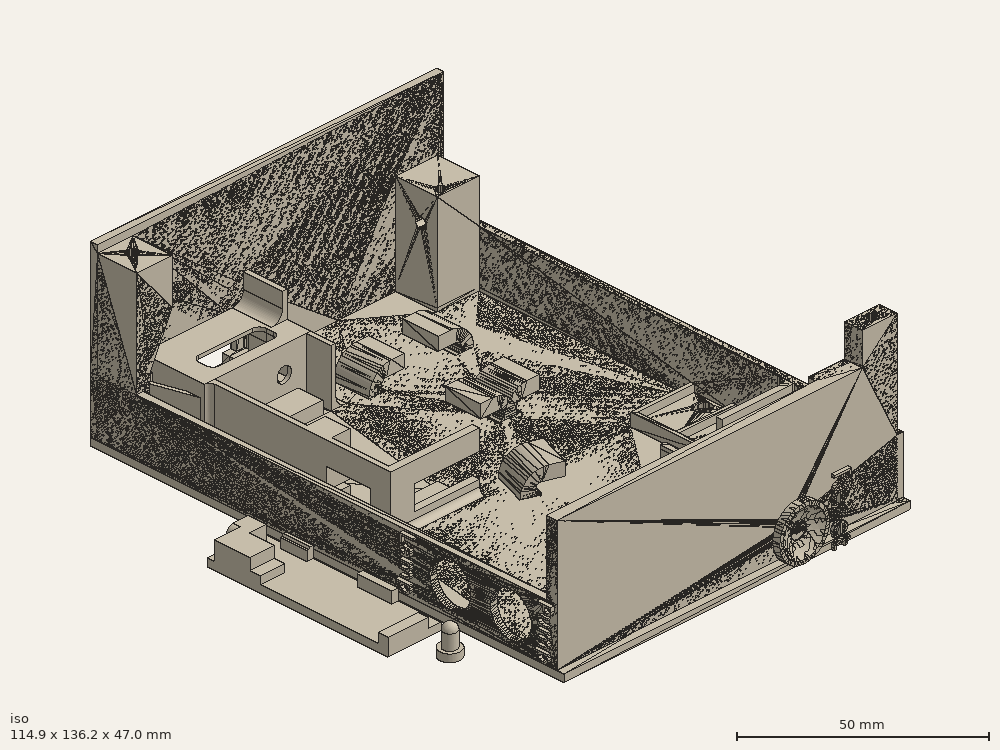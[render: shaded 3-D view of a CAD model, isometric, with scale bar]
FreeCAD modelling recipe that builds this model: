
FCSTD DOCUMENT  (FreeCAD 0.18.4R)
Label: tmp
License: All rights reserved
LicenseURL: http://en.wikipedia.org/wiki/All_rights_reserved
objects: Part::FeaturePython×102, Part::MultiFuse×20, Part::Part2DObjectPython×9, Part::Cut×8, Part::Extrusion×5, Part::Feature×5, App::DocumentObjectGroup×5, Part::Cone×4, Part::Fuse×1
note: 154 computed .brp shape members not serialized (recipe doc carries the construction recipe); baked Part::Feature solids carry a one-line shape summary decoded from their .brp

FEATURE [Part::FeaturePython] Slice002_child0  label="Slice002.0"  # WARN: FeaturePython — macro-defined, semantics opaque (R4)
  FilterType = 1
  Invert = false
  OverrideMaxVal = 0
  WindowFrom = 80
  WindowTo = 100
  items = 0
FEATURE [Part::FeaturePython] Slice005_child0  label="Slice005.0"  # WARN: FeaturePython — macro-defined, semantics opaque (R4)
  FilterType = 1
  Invert = false
  OverrideMaxVal = 0
  WindowFrom = 80
  WindowTo = 100
  items = 0
FEATURE [Part::Part2DObjectPython] Rectangle  # Draft 2D object (typed FeaturePython)
  ChamferSize = 0
  Columns = 1
  FilletRadius = 0
  Height = 55
  Length = 179
  MakeFace = true
  Placement = pos=(42.6826,-163.503,-171.403) rot=(-1,0,0;1.5708rad)
  Rows = 1
  Support = -> [Slice005_child0]
FEATURE [Part::FeaturePython] Slice  # WARN: FeaturePython — macro-defined, semantics opaque (R4)
  Base = -> Slice005_child0
  Mode = 1
  Tolerance = 0
  Tools = -> [Rectangle]
FEATURE [Part::FeaturePython] Slice_child0  label="Slice.0"  # WARN: FeaturePython — macro-defined, semantics opaque (R4)
  Base = -> Slice
  FilterType = 1
  Invert = false
  OverrideMaxVal = 0
  WindowFrom = 80
  WindowTo = 100
  items = 0
FEATURE [Part::FeaturePython] Slice_child1  label="Slice.1"  # WARN: FeaturePython — macro-defined, semantics opaque (R4)
  Base = -> Slice
  FilterType = 1
  Invert = false
  OverrideMaxVal = 0
  WindowFrom = 80
  WindowTo = 100
  items = 1
FEATURE [Part::FeaturePython] Slice_child2  label="Slice.2"  # WARN: FeaturePython — macro-defined, semantics opaque (R4)
  Base = -> Slice
  FilterType = 1
  Invert = false
  OverrideMaxVal = 0
  WindowFrom = 80
  WindowTo = 100
  items = 2
FEATURE [Part::FeaturePython] Slice003_child0  label="Side.1"  # WARN: FeaturePython — macro-defined, semantics opaque (R4)
  FilterType = 1
  Invert = false
  OverrideMaxVal = 0
  WindowFrom = 80
  WindowTo = 100
  items = 0
FEATURE [Part::FeaturePython] Slice002_child001  label="Slice002.001"  # WARN: FeaturePython — macro-defined, semantics opaque (R4)
  FilterType = 1
  Invert = false
  OverrideMaxVal = 0
  WindowFrom = 80
  WindowTo = 100
  items = 0
FEATURE [Part::FeaturePython] Slice_child5  label="Slice.5"  # WARN: FeaturePython — macro-defined, semantics opaque (R4)
  Base = -> Slice
  FilterType = 1
  Invert = false
  OverrideMaxVal = 0
  WindowFrom = 80
  WindowTo = 100
  items = 5
FEATURE [Part::FeaturePython] Slice_child8  label="Slice.8"  # WARN: FeaturePython — macro-defined, semantics opaque (R4)
  Base = -> Slice
  FilterType = 1
  Invert = false
  OverrideMaxVal = 0
  WindowFrom = 80
  WindowTo = 100
  items = 8
FEATURE [Part::FeaturePython] Slice_child009  label="Slice.009"  # WARN: FeaturePython — macro-defined, semantics opaque (R4)
  Base = -> Slice
  FilterType = 1
  Invert = false
  OverrideMaxVal = 0
  WindowFrom = 80
  WindowTo = 100
  items = 1
FEATURE [Part::FeaturePython] Slice_child3  label="Slice.3"  # WARN: FeaturePython — macro-defined, semantics opaque (R4)
  Base = -> Slice
  FilterType = 1
  Invert = false
  OverrideMaxVal = 0
  WindowFrom = 80
  WindowTo = 100
  items = 3
FEATURE [Part::FeaturePython] Slice002_child002  label="Slice002.002"  # WARN: FeaturePython — macro-defined, semantics opaque (R4)
  FilterType = 1
  Invert = false
  OverrideMaxVal = 0
  WindowFrom = 80
  WindowTo = 100
  items = 0
FEATURE [Part::FeaturePython] Slice_child6  label="Slice.6"  # WARN: FeaturePython — macro-defined, semantics opaque (R4)
  Base = -> Slice
  FilterType = 1
  Invert = false
  OverrideMaxVal = 0
  WindowFrom = 80
  WindowTo = 100
  items = 6
FEATURE [Part::FeaturePython] Slice_child7  label="Slice.7"  # WARN: FeaturePython — macro-defined, semantics opaque (R4)
  Base = -> Slice
  FilterType = 1
  Invert = false
  OverrideMaxVal = 0
  WindowFrom = 80
  WindowTo = 100
  items = 7
FEATURE [Part::FeaturePython] Slice_child010  label="Slice.010"  # WARN: FeaturePython — macro-defined, semantics opaque (R4)
  Base = -> Slice
  FilterType = 1
  Invert = false
  OverrideMaxVal = 0
  WindowFrom = 80
  WindowTo = 100
  items = 2
FEATURE [Part::FeaturePython] Slice_child4  label="Slice.4"  # WARN: FeaturePython — macro-defined, semantics opaque (R4)
  Base = -> Slice
  FilterType = 1
  Invert = false
  OverrideMaxVal = 0
  WindowFrom = 80
  WindowTo = 100
  items = 4
FEATURE [Part::FeaturePython] Slice002_child003  label="Slice002.003"  # WARN: FeaturePython — macro-defined, semantics opaque (R4)
  FilterType = 1
  Invert = false
  OverrideMaxVal = 0
  WindowFrom = 80
  WindowTo = 100
  items = 0
FEATURE [Part::FeaturePython] Slice001_child1  label="Slice001.1"  # WARN: FeaturePython — macro-defined, semantics opaque (R4)
  FilterType = 1
  Invert = false
  OverrideMaxVal = 0
  WindowFrom = 80
  WindowTo = 100
  items = 1
FEATURE [Part::FeaturePython] Slice002_child004  label="Slice002.004"  # WARN: FeaturePython — macro-defined, semantics opaque (R4)
  FilterType = 1
  Invert = false
  OverrideMaxVal = 0
  WindowFrom = 80
  WindowTo = 100
  items = 0
FEATURE [Part::FeaturePython] Slice001_child2  label="Slice001.2"  # WARN: FeaturePython — macro-defined, semantics opaque (R4)
  FilterType = 1
  Invert = false
  OverrideMaxVal = 0
  WindowFrom = 80
  WindowTo = 100
  items = 2
FEATURE [Part::FeaturePython] Slice001_child5  label="Slice001.5"  # WARN: FeaturePython — macro-defined, semantics opaque (R4)
  FilterType = 1
  Invert = false
  OverrideMaxVal = 0
  WindowFrom = 80
  WindowTo = 100
  items = 5
FEATURE [Part::FeaturePython] Slice001_child4  label="Slice001.4"  # WARN: FeaturePython — macro-defined, semantics opaque (R4)
  FilterType = 1
  Invert = false
  OverrideMaxVal = 0
  WindowFrom = 80
  WindowTo = 100
  items = 4
FEATURE [Part::FeaturePython] Slice001_child3  label="Slice001.3"  # WARN: FeaturePython — macro-defined, semantics opaque (R4)
  FilterType = 1
  Invert = false
  OverrideMaxVal = 0
  WindowFrom = 80
  WindowTo = 100
  items = 3
FEATURE [Part::FeaturePython] Slice001_child6  label="Slice001.6"  # WARN: FeaturePython — macro-defined, semantics opaque (R4)
  FilterType = 1
  Invert = false
  OverrideMaxVal = 0
  WindowFrom = 80
  WindowTo = 100
  items = 6
FEATURE [Part::FeaturePython] Slice002_child005  label="Slice002.005"  # WARN: FeaturePython — macro-defined, semantics opaque (R4)
  FilterType = 1
  Invert = false
  OverrideMaxVal = 0
  WindowFrom = 80
  WindowTo = 100
  items = 0
FEATURE [Part::FeaturePython] Slice004_child2  label="Slice004.2"  # WARN: FeaturePython — macro-defined, semantics opaque (R4)
  FilterType = 1
  Invert = false
  OverrideMaxVal = 0
  WindowFrom = 80
  WindowTo = 100
  items = 2
FEATURE [Part::FeaturePython] Slice002_child006  label="Slice002.006"  # WARN: FeaturePython — macro-defined, semantics opaque (R4)
  FilterType = 1
  Invert = false
  OverrideMaxVal = 0
  WindowFrom = 80
  WindowTo = 100
  items = 0
FEATURE [Part::FeaturePython] Slice004_child0  label="Slice004.0"  # WARN: FeaturePython — macro-defined, semantics opaque (R4)
  FilterType = 1
  Invert = false
  OverrideMaxVal = 0
  WindowFrom = 80
  WindowTo = 100
  items = 0
FEATURE [Part::FeaturePython] Slice002_child007  label="Slice002.007"  # WARN: FeaturePython — macro-defined, semantics opaque (R4)
  FilterType = 1
  Invert = false
  OverrideMaxVal = 0
  WindowFrom = 80
  WindowTo = 100
  items = 0
FEATURE [Part::FeaturePython] Slice004_child1  label="Slice004.1"  # WARN: FeaturePython — macro-defined, semantics opaque (R4)
  FilterType = 1
  Invert = false
  OverrideMaxVal = 0
  WindowFrom = 80
  WindowTo = 100
  items = 1
FEATURE [Part::FeaturePython] Slice002_child008  label="Slice002.008"  # WARN: FeaturePython — macro-defined, semantics opaque (R4)
  FilterType = 1
  Invert = false
  OverrideMaxVal = 0
  WindowFrom = 80
  WindowTo = 100
  items = 0
FEATURE [Part::MultiFuse] Fusion005002002014004003003002009002010004002003006003008008004007002004008002005011010
  Placement = pos=(0,2,-7.6398e-11) rot=(0,0,1;0rad)
FEATURE [Part::FeaturePython] Slice002_child009  label="Slice002.009"  # WARN: FeaturePython — macro-defined, semantics opaque (R4)
  FilterType = 1
  Invert = false
  OverrideMaxVal = 0
  WindowFrom = 80
  WindowTo = 100
  items = 0
FEATURE [Part::Part2DObjectPython] Rectangle001  # Draft 2D object (typed FeaturePython)
  ChamferSize = 0
  Columns = 1
  FilletRadius = 0
  Height = 2
  Length = 19
  MakeFace = true
  Placement = pos=(97.4504,-49.8028,-174.501) rot=(0,0,1;0rad)
  Rows = 1
  Support = -> [Slice004_child0]
FEATURE [Part::Extrusion] Extrusion
  Base = -> Rectangle001
  Dir = (-2.94077e-10,-1.24144e-10,-3.25)
  DirMode = 0
  FaceMakerClass = Part::FaceMakerBullseye
  LengthFwd = 0
  LengthRev = 0
  Solid = true
  Symmetric = false
FEATURE [Part::Cut] Cut
  Base = -> Slice004_child0
  Tool = -> Extrusion
FEATURE [Part::Cut] Cut001  label="Connector.2"
  Base = -> Cut
  Tool = -> Fusion005002002014004003003002009002010004002003006003008008004007002004008002005011010
FEATURE [Part::FeaturePython] Slice003_child6  label="Slice003.6"  # WARN: FeaturePython — macro-defined, semantics opaque (R4)
  FilterType = 1
  Invert = false
  OverrideMaxVal = 0
  WindowFrom = 80
  WindowTo = 100
  items = 6
FEATURE [Part::FeaturePython] Slice003_child3  label="Slice003.3"  # WARN: FeaturePython — macro-defined, semantics opaque (R4)
  FilterType = 1
  Invert = false
  OverrideMaxVal = 0
  WindowFrom = 80
  WindowTo = 100
  items = 3
FEATURE [Part::FeaturePython] Slice003_child2  label="Slice003.2"  # WARN: FeaturePython — macro-defined, semantics opaque (R4)
  FilterType = 1
  Invert = false
  OverrideMaxVal = 0
  WindowFrom = 80
  WindowTo = 100
  items = 2
FEATURE [Part::FeaturePython] Slice003_child5  label="Slice003.5"  # WARN: FeaturePython — macro-defined, semantics opaque (R4)
  FilterType = 1
  Invert = false
  OverrideMaxVal = 0
  WindowFrom = 80
  WindowTo = 100
  items = 5
FEATURE [Part::FeaturePython] Slice003_child4  label="Slice003.4"  # WARN: FeaturePython — macro-defined, semantics opaque (R4)
  FilterType = 1
  Invert = false
  OverrideMaxVal = 0
  WindowFrom = 80
  WindowTo = 100
  items = 4
FEATURE [Part::FeaturePython] Slice003_child1  label="Slice003.1"  # WARN: FeaturePython — macro-defined, semantics opaque (R4)
  FilterType = 1
  Invert = false
  OverrideMaxVal = 0
  WindowFrom = 80
  WindowTo = 100
  items = 1
FEATURE [Part::Cone] Cone001
  Angle = 360
  AttacherType = Attacher::AttachEngine3D
  Height = 1.5
  Placement = pos=(168.62,-144.553,-191.501) rot=(0,0,1;0rad)
  Radius1 = 3
  Radius2 = 1.5
FEATURE [Part::Cut] Cut002
  Base = -> Slice002_child009
  Tool = -> Cone001
FEATURE [Part::FeaturePython] Slice003_child007  label="Slice003.007"  # WARN: FeaturePython — macro-defined, semantics opaque (R4)
  FilterType = 1
  Invert = false
  OverrideMaxVal = 0
  WindowFrom = 80
  WindowTo = 100
  items = 3
FEATURE [Part::FeaturePython] Slice003_child008  label="Slice003.008"  # WARN: FeaturePython — macro-defined, semantics opaque (R4)
  FilterType = 1
  Invert = false
  OverrideMaxVal = 0
  WindowFrom = 80
  WindowTo = 100
  items = 2
FEATURE [Part::FeaturePython] Slice003_child009  label="Slice003.009"  # WARN: FeaturePython — macro-defined, semantics opaque (R4)
  FilterType = 1
  Invert = false
  OverrideMaxVal = 0
  WindowFrom = 80
  WindowTo = 100
  items = 0
FEATURE [Part::FeaturePython] Slice003_child010  label="Slice003.010"  # WARN: FeaturePython — macro-defined, semantics opaque (R4)
  FilterType = 1
  Invert = false
  OverrideMaxVal = 0
  WindowFrom = 80
  WindowTo = 100
  items = 1
FEATURE [Part::Cone] Cone002
  Angle = 360
  AttacherType = Attacher::AttachEngine3D
  Height = 2
  Placement = pos=(166.12,-47.2028,-191.501) rot=(0,0,1;0rad)
  Radius1 = 3
  Radius2 = 1.4
FEATURE [Part::Cut] Cut003
  Base = -> Cut002
  Tool = -> Cone002
FEATURE [Part::Part2DObjectPython] Wire  # Draft 2D object (typed FeaturePython)
  ChamferSize = 0
  Closed = true
  End = (81.4504,-48.3028,-174.501)
  FilletRadius = 0
  Length = 38.5771
  MakeFace = true
  Placement = pos=(81.4504,-48.3028,-189.501) rot=(0.57735,0.57735,0.57735;2.0944rad)
  Points = (3) [(0,0,0),(6.40156e-10,19,2),(5.65358e-10,15,2.17554e-10)]
  Start = (81.4504,-48.3028,-189.501)
  Subdivisions = 0
FEATURE [Part::Extrusion] Extrusion001
  Base = -> Wire
  Dir = (4.17798e-10,11,-4.14596e-10)
  DirMode = 0
  FaceMakerClass = Part::FaceMakerBullseye
  LengthFwd = 0
  LengthRev = 0
  Solid = true
  Symmetric = false
FEATURE [Part::MultiFuse] Fusion
  Shapes = -> [Slice_child1,Extrusion001]
FEATURE [Part::Feature] Fusion005002002014004003003002009002010004002003006003008008004007002004008002005001  label="PowerSupply-cover"
  shape: bbox 14.8 x 50.9 x 7 mm, 30 faces (baked)
FEATURE [Part::MultiFuse] Fusion005002002014004003003002009002010004002003006003008008004007002004008002005011006  label="Button"
  Placement = pos=(371.865,-232.312,-185.367) rot=(0,0,1;0rad)
FEATURE [Part::FeaturePython] Slice002_child010  label="Slice002.010"  # WARN: FeaturePython — macro-defined, semantics opaque (R4)
  FilterType = 1
  Invert = false
  OverrideMaxVal = 0
  WindowFrom = 80
  WindowTo = 100
  items = 0
FEATURE [Part::FeaturePython] Slice003_child011  label="Frame-1side"  # WARN: FeaturePython — macro-defined, semantics opaque (R4)
  FilterType = 1
  Invert = false
  OverrideMaxVal = 0
  WindowFrom = 80
  WindowTo = 100
  items = 0
FEATURE [Part::FeaturePython] Slice001_child007  label="Slice001.007"  # WARN: FeaturePython — macro-defined, semantics opaque (R4)
  FilterType = 1
  Invert = false
  OverrideMaxVal = 0
  WindowFrom = 80
  WindowTo = 100
  items = 3
FEATURE [Part::FeaturePython] Slice003_child012  label="Slice003.012"  # WARN: FeaturePython — macro-defined, semantics opaque (R4)
  FilterType = 1
  Invert = false
  OverrideMaxVal = 0
  WindowFrom = 80
  WindowTo = 100
  items = 2
FEATURE [Part::FeaturePython] Slice003_child013  label="Slice003.013"  # WARN: FeaturePython — macro-defined, semantics opaque (R4)
  FilterType = 1
  Invert = false
  OverrideMaxVal = 0
  WindowFrom = 80
  WindowTo = 100
  items = 4
FEATURE [Part::FeaturePython] Slice003_child014  label="Slice003.014"  # WARN: FeaturePython — macro-defined, semantics opaque (R4)
  FilterType = 1
  Invert = false
  OverrideMaxVal = 0
  WindowFrom = 80
  WindowTo = 100
  items = 1
FEATURE [Part::FeaturePython] Slice005_child001  label="Slice005.001"  # WARN: FeaturePython — macro-defined, semantics opaque (R4)
  FilterType = 1
  Invert = false
  OverrideMaxVal = 0
  WindowFrom = 80
  WindowTo = 100
  items = 0
FEATURE [Part::FeaturePython] Slice002_child011  label="Slice002.011"  # WARN: FeaturePython — macro-defined, semantics opaque (R4)
  FilterType = 1
  Invert = false
  OverrideMaxVal = 0
  WindowFrom = 80
  WindowTo = 100
  items = 0
FEATURE [Part::Part2DObjectPython] Rectangle002  # Draft 2D object (typed FeaturePython)
  ChamferSize = 0
  Columns = 1
  FilletRadius = 0
  Height = 55
  Length = 179
  MakeFace = true
  Placement = pos=(42.6826,-163.503,-171.403) rot=(-1,0,0;1.5708rad)
  Rows = 1
  Support = -> [Slice005_child001]
FEATURE [Part::FeaturePython] Slice002_child012  label="Slice002.012"  # WARN: FeaturePython — macro-defined, semantics opaque (R4)
  FilterType = 1
  Invert = false
  OverrideMaxVal = 0
  WindowFrom = 80
  WindowTo = 100
  items = 0
FEATURE [Part::FeaturePython] Slice003_child015  label="Slice003.015"  # WARN: FeaturePython — macro-defined, semantics opaque (R4)
  FilterType = 1
  Invert = false
  OverrideMaxVal = 0
  WindowFrom = 80
  WindowTo = 100
  items = 1
FEATURE [Part::FeaturePython] Slice001  # WARN: FeaturePython — macro-defined, semantics opaque (R4)
  Base = -> Slice005_child001
  Mode = 1
  Tolerance = 0
  Tools = -> [Rectangle002]
FEATURE [Part::FeaturePython] Slice_child011  label="Slice.011"  # WARN: FeaturePython — macro-defined, semantics opaque (R4)
  Base = -> Slice001
  FilterType = 1
  Invert = false
  OverrideMaxVal = 0
  WindowFrom = 80
  WindowTo = 100
  items = 6
FEATURE [Part::FeaturePython] Slice_child012  label="Slice.012"  # WARN: FeaturePython — macro-defined, semantics opaque (R4)
  Base = -> Slice001
  FilterType = 1
  Invert = false
  OverrideMaxVal = 0
  WindowFrom = 80
  WindowTo = 100
  items = 1
FEATURE [Part::FeaturePython] Slice_child013  label="Slice.013"  # WARN: FeaturePython — macro-defined, semantics opaque (R4)
  Base = -> Slice001
  FilterType = 1
  Invert = false
  OverrideMaxVal = 0
  WindowFrom = 80
  WindowTo = 100
  items = 5
FEATURE [Part::FeaturePython] Slice_child014  label="Slice.014"  # WARN: FeaturePython — macro-defined, semantics opaque (R4)
  Base = -> Slice001
  FilterType = 1
  Invert = false
  OverrideMaxVal = 0
  WindowFrom = 80
  WindowTo = 100
  items = 2
FEATURE [Part::FeaturePython] Slice_child015  label="Slice.015"  # WARN: FeaturePython — macro-defined, semantics opaque (R4)
  Base = -> Slice001
  FilterType = 1
  Invert = false
  OverrideMaxVal = 0
  WindowFrom = 80
  WindowTo = 100
  items = 0
FEATURE [Part::FeaturePython] Slice_child016  label="Slice.016"  # WARN: FeaturePython — macro-defined, semantics opaque (R4)
  Base = -> Slice001
  FilterType = 1
  Invert = false
  OverrideMaxVal = 0
  WindowFrom = 80
  WindowTo = 100
  items = 3
FEATURE [Part::FeaturePython] Slice_child017  label="Slice.017"  # WARN: FeaturePython — macro-defined, semantics opaque (R4)
  Base = -> Slice001
  FilterType = 1
  Invert = false
  OverrideMaxVal = 0
  WindowFrom = 80
  WindowTo = 100
  items = 8
FEATURE [Part::FeaturePython] Slice_child018  label="Slice.018"  # WARN: FeaturePython — macro-defined, semantics opaque (R4)
  Base = -> Slice001
  FilterType = 1
  Invert = false
  OverrideMaxVal = 0
  WindowFrom = 80
  WindowTo = 100
  items = 1
FEATURE [Part::FeaturePython] Slice002_child013  label="Slice002.013"  # WARN: FeaturePython — macro-defined, semantics opaque (R4)
  FilterType = 1
  Invert = false
  OverrideMaxVal = 0
  WindowFrom = 80
  WindowTo = 100
  items = 0
FEATURE [Part::FeaturePython] Slice_child019  label="Slice.019"  # WARN: FeaturePython — macro-defined, semantics opaque (R4)
  Base = -> Slice001
  FilterType = 1
  Invert = false
  OverrideMaxVal = 0
  WindowFrom = 80
  WindowTo = 100
  items = 7
FEATURE [Part::FeaturePython] Slice002_child014  label="Slice002.014"  # WARN: FeaturePython — macro-defined, semantics opaque (R4)
  FilterType = 1
  Invert = false
  OverrideMaxVal = 0
  WindowFrom = 80
  WindowTo = 100
  items = 0
FEATURE [Part::FeaturePython] Slice002_child015  label="Slice002.015"  # WARN: FeaturePython — macro-defined, semantics opaque (R4)
  FilterType = 1
  Invert = false
  OverrideMaxVal = 0
  WindowFrom = 80
  WindowTo = 100
  items = 0
FEATURE [Part::FeaturePython] Slice_child020  label="Slice.020"  # WARN: FeaturePython — macro-defined, semantics opaque (R4)
  Base = -> Slice001
  FilterType = 1
  Invert = false
  OverrideMaxVal = 0
  WindowFrom = 80
  WindowTo = 100
  items = 4
FEATURE [Part::FeaturePython] Slice_child021  label="Slice.021"  # WARN: FeaturePython — macro-defined, semantics opaque (R4)
  Base = -> Slice001
  FilterType = 1
  Invert = false
  OverrideMaxVal = 0
  WindowFrom = 80
  WindowTo = 100
  items = 2
FEATURE [Part::FeaturePython] Slice001_child008  label="Slice001.008"  # WARN: FeaturePython — macro-defined, semantics opaque (R4)
  FilterType = 1
  Invert = false
  OverrideMaxVal = 0
  WindowFrom = 80
  WindowTo = 100
  items = 1
FEATURE [Part::FeaturePython] Slice004_child003  label="Slice004.003"  # WARN: FeaturePython — macro-defined, semantics opaque (R4)
  FilterType = 1
  Invert = false
  OverrideMaxVal = 0
  WindowFrom = 80
  WindowTo = 100
  items = 2
FEATURE [Part::FeaturePython] Slice001_child009  label="Slice001.009"  # WARN: FeaturePython — macro-defined, semantics opaque (R4)
  FilterType = 1
  Invert = false
  OverrideMaxVal = 0
  WindowFrom = 80
  WindowTo = 100
  items = 2
FEATURE [Part::FeaturePython] Slice001_child010  label="Slice001.010"  # WARN: FeaturePython — macro-defined, semantics opaque (R4)
  FilterType = 1
  Invert = false
  OverrideMaxVal = 0
  WindowFrom = 80
  WindowTo = 100
  items = 6
FEATURE [Part::FeaturePython] Slice001_child011  label="Slice001.011"  # WARN: FeaturePython — macro-defined, semantics opaque (R4)
  FilterType = 1
  Invert = false
  OverrideMaxVal = 0
  WindowFrom = 80
  WindowTo = 100
  items = 5
FEATURE [Part::FeaturePython] Slice001_child012  label="Slice001.012"  # WARN: FeaturePython — macro-defined, semantics opaque (R4)
  FilterType = 1
  Invert = false
  OverrideMaxVal = 0
  WindowFrom = 80
  WindowTo = 100
  items = 4
FEATURE [Part::FeaturePython] Slice002_child016  label="Slice002.016"  # WARN: FeaturePython — macro-defined, semantics opaque (R4)
  FilterType = 1
  Invert = false
  OverrideMaxVal = 0
  WindowFrom = 80
  WindowTo = 100
  items = 0
FEATURE [Part::MultiFuse] Fusion005002002014004003003002009002010004002003006003008008004007002004008002005011011
  Placement = pos=(0,2,-7.6398e-11) rot=(0,0,1;0rad)
FEATURE [Part::FeaturePython] Slice004_child004  label="Slice004.004"  # WARN: FeaturePython — macro-defined, semantics opaque (R4)
  FilterType = 1
  Invert = false
  OverrideMaxVal = 0
  WindowFrom = 80
  WindowTo = 100
  items = 1
FEATURE [Part::FeaturePython] Slice004_child005  label="Slice004.005"  # WARN: FeaturePython — macro-defined, semantics opaque (R4)
  FilterType = 1
  Invert = false
  OverrideMaxVal = 0
  WindowFrom = 80
  WindowTo = 100
  items = 0
FEATURE [Part::FeaturePython] Slice002_child017  label="Slice002.017"  # WARN: FeaturePython — macro-defined, semantics opaque (R4)
  FilterType = 1
  Invert = false
  OverrideMaxVal = 0
  WindowFrom = 80
  WindowTo = 100
  items = 0
FEATURE [Part::Part2DObjectPython] Rectangle003  # Draft 2D object (typed FeaturePython)
  ChamferSize = 0
  Columns = 1
  FilletRadius = 0
  Height = 2
  Length = 19
  MakeFace = true
  Placement = pos=(97.4504,-49.8028,-174.501) rot=(0,0,1;0rad)
  Rows = 1
  Support = -> [Slice004_child005]
FEATURE [Part::FeaturePython] Slice002_child018  label="Slice002.018"  # WARN: FeaturePython — macro-defined, semantics opaque (R4)
  FilterType = 1
  Invert = false
  OverrideMaxVal = 0
  WindowFrom = 80
  WindowTo = 100
  items = 0
FEATURE [Part::FeaturePython] Slice002_child019  label="Slice002.019"  # WARN: FeaturePython — macro-defined, semantics opaque (R4)
  FilterType = 1
  Invert = false
  OverrideMaxVal = 0
  WindowFrom = 80
  WindowTo = 100
  items = 0
FEATURE [Part::FeaturePython] Slice003_child016  label="Slice003.016"  # WARN: FeaturePython — macro-defined, semantics opaque (R4)
  FilterType = 1
  Invert = false
  OverrideMaxVal = 0
  WindowFrom = 80
  WindowTo = 100
  items = 3
FEATURE [Part::FeaturePython] Slice003_child017  label="Slice003.017"  # WARN: FeaturePython — macro-defined, semantics opaque (R4)
  FilterType = 1
  Invert = false
  OverrideMaxVal = 0
  WindowFrom = 80
  WindowTo = 100
  items = 3
FEATURE [Part::Extrusion] Extrusion002
  Base = -> Rectangle003
  Dir = (-2.94077e-10,-1.24144e-10,-3.25)
  DirMode = 0
  FaceMakerClass = Part::FaceMakerBullseye
  LengthFwd = 0
  LengthRev = 0
  Solid = true
  Symmetric = false
FEATURE [Part::Cut] Cut006
  Base = -> Slice004_child005
  Tool = -> Extrusion002
FEATURE [Part::Cut] Cut005  label="Connector.box"
  Base = -> Cut006
  Tool = -> Fusion005002002014004003003002009002010004002003006003008008004007002004008002005011011
FEATURE [Part::FeaturePython] Slice003_child018  label="Reset-Cover"  # WARN: FeaturePython — macro-defined, semantics opaque (R4)
  FilterType = 1
  Invert = false
  OverrideMaxVal = 0
  WindowFrom = 80
  WindowTo = 100
  items = 6
FEATURE [Part::FeaturePython] Slice003_child019  label="Slice003.019"  # WARN: FeaturePython — macro-defined, semantics opaque (R4)
  FilterType = 1
  Invert = false
  OverrideMaxVal = 0
  WindowFrom = 80
  WindowTo = 100
  items = 0
FEATURE [Part::Cone] Cone003
  Angle = 360
  AttacherType = Attacher::AttachEngine3D
  Height = 1.5
  Placement = pos=(168.62,-144.553,-191.501) rot=(0,0,1;0rad)
  Radius1 = 3
  Radius2 = 1.5
FEATURE [Part::Cut] Cut004
  Base = -> Slice002_child019
  Tool = -> Cone003
FEATURE [Part::FeaturePython] Slice003_child020  label="Slice003.020"  # WARN: FeaturePython — macro-defined, semantics opaque (R4)
  FilterType = 1
  Invert = false
  OverrideMaxVal = 0
  WindowFrom = 80
  WindowTo = 100
  items = 5
FEATURE [Part::Cone] Cone004
  Angle = 360
  AttacherType = Attacher::AttachEngine3D
  Height = 2
  Placement = pos=(166.12,-47.2028,-191.501) rot=(0,0,1;0rad)
  Radius1 = 3
  Radius2 = 1.4
FEATURE [Part::Cut] Cut007  label="Bottom"
  Base = -> Cut004
  Tool = -> Cone004
FEATURE [Part::Part2DObjectPython] Wire001  # Draft 2D object (typed FeaturePython)
  ChamferSize = 0
  Closed = true
  End = (81.4504,-48.3028,-174.501)
  FilletRadius = 0
  Length = 38.5771
  MakeFace = true
  Placement = pos=(81.4504,-48.3028,-189.501) rot=(0.57735,0.57735,0.57735;2.0944rad)
  Points = (3) [(0,0,0),(6.40156e-10,19,2),(5.65358e-10,15,2.17554e-10)]
  Start = (81.4504,-48.3028,-189.501)
  Subdivisions = 0
FEATURE [Part::Extrusion] Extrusion003
  Base = -> Wire001
  Dir = (4.17798e-10,11,-4.14596e-10)
  DirMode = 0
  FaceMakerClass = Part::FaceMakerBullseye
  LengthFwd = 0
  LengthRev = 0
  Solid = true
  Symmetric = false
FEATURE [Part::MultiFuse] Fusion005002002014004003003002009002010004002003006003008008004007002004008002005011012
  Shapes = -> [Slice_child012,Extrusion003]
FEATURE [Part::FeaturePython] Slice003_child021  label="Slice003.021"  # WARN: FeaturePython — macro-defined, semantics opaque (R4)
  FilterType = 1
  Invert = false
  OverrideMaxVal = 0
  WindowFrom = 80
  WindowTo = 100
  items = 2
FEATURE [Part::MultiFuse] Fusion005002002014004003003002009002010004002003006003008008004007002004008002005011013  label="clamps"
  Shapes = -> [Slice003_child014,Slice003_child019,Slice003_child021,Slice003_child017]
FEATURE [Part::MultiFuse] Fusion005002002014004003003002009002010004002003006003008008004007002004008002005011014  label="powersupplay.box"
  Shapes = -> [Slice004_child003,Slice004_child004]
FEATURE [Part::MultiFuse] Fusion005002002014004003003002009002010004002003006003008008004007002004008002005011015  label="Title-AC230V"
  Shapes = -> [Slice001_child008,Slice001_child009,Slice001_child011,Slice001_child012,Slice001_child007,Slice001_child010]
FEATURE [Part::MultiFuse] Fusion005002002014004003003002009002010004002003006003008008004007002004008002005011016  label="Title-Lamp"
  Shapes = -> [Slice_child011,Slice_child019,Slice_child021,Slice_child020]
FEATURE [Part::MultiFuse] Fusion005002002014004003003002009002010004002003006003008008004007002004008002005011017  label="Title-Pump"
  Shapes = -> [Slice_child013,Slice_child017,Slice_child018,Slice_child016]
FEATURE [Part::MultiFuse] Fusion005002002014004003003002009002010004002003006003008008004007002004008002005011018  label="Title-Reset"
  Shapes = -> [Slice003_child016,Slice003_child012,Slice003_child020,Slice003_child013,Slice003_child015]
FEATURE [Part::MultiFuse] Fusion005002002014004003003002009002010004002003006003008008004007002004008002005011019
  Shapes = -> [Slice003_child011,Slice_child015]
FEATURE [Part::MultiFuse] Fusion005002002014004003003002009002010004002003006003008008004007002004008002005011020  label="Bottot.2"
  Shapes = -> [Slice003_child007,Slice003_child008,Slice003_child009,Slice003_child010,Cut003]
FEATURE [Part::MultiFuse] Fusion005002002014004003003002009002010004002003006003008008004007002004008002005011021  label="Reset.2"
  Shapes = -> [Slice003_child6,Slice003_child3,Slice003_child2,Slice003_child5,Slice003_child4,Slice003_child1]
FEATURE [Part::MultiFuse] Fusion005002002014004003003002009002010004002003006003008008004007002004008002005011022  label="Power.Supply"
  Shapes = -> [Slice004_child2,Slice004_child1]
FEATURE [Part::MultiFuse] Fusion005002002014004003003002009002010004002003006003008008004007002004008002005011023  label="AC230V"
  Shapes = -> [Slice001_child1,Slice001_child2,Slice001_child5,Slice001_child4,Slice001_child3,Slice001_child6]
FEATURE [Part::MultiFuse] Fusion005002002014004003003002009002010004002003006003008008004007002004008002005011024  label="Lamp"
  Shapes = -> [Slice_child6,Slice_child010,Slice_child4,Slice_child7]
FEATURE [Part::MultiFuse] Fusion005002002014004003003002009002010004002003006003008008004007002004008002005011025  label="Pump"
  Shapes = -> [Slice_child5,Slice_child8,Slice_child009,Slice_child3]
FEATURE [Part::FeaturePython] BooleanFragments  # WARN: FeaturePython — macro-defined, semantics opaque (R4)
  Mode = 0
  Objects = -> [Fusion005002002014004003003002009002010004002003006003008008004007002004008002005011012,Slice003_child0]
  Tolerance = 0
FEATURE [Part::Feature] Fusion005002002014004003003002009002010004002003006003008008004007002004008002005011019001  label="sides-2"
  shape: bbox 97.4 x 131.2 x 45 mm, 59 faces, 2 solids (baked)
FEATURE [Part::MultiFuse] Fusion005002002014004003003002009002010004002003006003008008004007002004008002005011019002
  Shapes = -> [Fusion005002002014004003003002009002010004002003006003008008004007002004008002005011012,Fusion005002002014004003003002009002010004002003006003008008004007002004008002005011019001]
FEATURE [App::DocumentObjectGroup] GrExplode_Slice001  label="Frame-3side"
  Group = -> [Slice_child014,Fusion005002002014004003003002009002010004002003006003008008004007002004008002005011019,Fusion005002002014004003003002009002010004002003006003008008004007002004008002005011019002]
FEATURE [App::DocumentObjectGroup] GrExplode_Slice  label="Exploded Slice"
  Group = -> [Slice_child0,Slice_child2,Fusion,Slice002_child012,Slice002_child015,Slice002_child014,Slice002_child016,Slice002_child013,Cut005,Slice003_child018,Slice002_child017,Cut007,GrExplode_Slice001,Slice002_child011,Slice002_child018,Slice002_child010,Fusion005002002014004003003002009002010004002003006003008008004007002004008002005011006,+7 more]
FEATURE [Part::Feature] Fusion005002002014004003003002009002010004002003006003008008004007002004008002005011019002001  label="sides-3"
  shape: bbox 97.4 x 131.2 x 45 mm, 68 faces (baked)
FEATURE [Part::Part2DObjectPython] Rectangle004  # Draft 2D object (typed FeaturePython)
  ChamferSize = 0
  Columns = 1
  FilletRadius = 0
  Height = 99
  Length = 175
  MakeFace = true
  Placement = pos=(175.12,-20.86,-220.773) rot=(0.57735,-0.57735,-0.57735;2.0944rad)
  Rows = 1
  Support = -> [Slice_child014]
FEATURE [Part::FeaturePython] Slice002  # WARN: FeaturePython — macro-defined, semantics opaque (R4)
  Base = -> Slice_child014
  Mode = 1
  Tolerance = 0
  Tools = -> [Rectangle004]
FEATURE [Part::FeaturePython] Slice002_child0020  label="Slice002.020"  # WARN: FeaturePython — macro-defined, semantics opaque (R4)
  Base = -> Slice002
  FilterType = 1
  Invert = false
  OverrideMaxVal = 0
  WindowFrom = 80
  WindowTo = 100
  items = 0
FEATURE [Part::FeaturePython] Slice002_child1  label="Slice002.1"  # WARN: FeaturePython — macro-defined, semantics opaque (R4)
  Base = -> Slice002
  FilterType = 1
  Invert = false
  OverrideMaxVal = 0
  WindowFrom = 80
  WindowTo = 100
  items = 1
FEATURE [Part::FeaturePython] Slice002_child2  label="Slice002.2"  # WARN: FeaturePython — macro-defined, semantics opaque (R4)
  Base = -> Slice002
  FilterType = 1
  Invert = false
  OverrideMaxVal = 0
  WindowFrom = 80
  WindowTo = 100
  items = 2
FEATURE [Part::FeaturePython] Slice002_child3  label="Slice002.3"  # WARN: FeaturePython — macro-defined, semantics opaque (R4)
  Base = -> Slice002
  FilterType = 1
  Invert = false
  OverrideMaxVal = 0
  WindowFrom = 80
  WindowTo = 100
  items = 3
FEATURE [Part::FeaturePython] Slice002_child4  label="Slice002.4"  # WARN: FeaturePython — macro-defined, semantics opaque (R4)
  Base = -> Slice002
  FilterType = 1
  Invert = false
  OverrideMaxVal = 0
  WindowFrom = 80
  WindowTo = 100
  items = 4
FEATURE [Part::MultiFuse] Fusion005002002014004003003002009002010004002003006003008008004007002004008002005011019002002
  Shapes = -> [Slice002_child2,Fusion005002002014004003003002009002010004002003006003008008004007002004008002005011019002001]
FEATURE [Part::Feature] Fusion005002002014004003003002009002010004002003006003008008004007002004008002005011019002002001  label="Framee"
  shape: bbox 97.4 x 131.2 x 45 mm, 72 faces (baked)
FEATURE [Part::Fuse] Fusion005002002014004003003002009002010004002003006003008008004007002004008002005011019002002002
  Base = -> Slice002_child3
  Tool = -> Fusion005002002014004003003002009002010004002003006003008008004007002004008002005011019002002001
FEATURE [App::DocumentObjectGroup] GrExplode_Slice002  label="Exploded Slice002"
  Group = -> [Slice002_child0020,Slice002_child1,Slice002_child4,Fusion005002002014004003003002009002010004002003006003008008004007002004008002005011019002002,Fusion005002002014004003003002009002010004002003006003008008004007002004008002005011019002002002]
FEATURE [Part::Feature] Fusion005002002014004003003002009002010004002003006003008008004007002004008002005011019002002002001  label="Frame"
  shape: bbox 97.4 x 131.2 x 45 mm, 79 faces (baked)
FEATURE [Part::Part2DObjectPython] Rectangle005  # Draft 2D object (typed FeaturePython)
  ChamferSize = 0
  Columns = 1
  FilletRadius = 0
  Height = 134
  Length = 168
  MakeFace = true
  Placement = pos=(175.12,-18.86,-272.773) rot=(0.57735,-0.57735,-0.57735;2.0944rad)
  Rows = 1
  Support = -> [Slice005_child001]
FEATURE [Part::FeaturePython] Slice003  # WARN: FeaturePython — macro-defined, semantics opaque (R4)
  Base = -> Slice005_child001
  Mode = 1
  Tolerance = 0
  Tools = -> [Rectangle005]
FEATURE [Part::FeaturePython] Slice003_child0022  label="Slice003.0"  # WARN: FeaturePython — macro-defined, semantics opaque (R4)
  Base = -> Slice003
  FilterType = 1
  Invert = false
  OverrideMaxVal = 0
  WindowFrom = 80
  WindowTo = 100
  items = 0
FEATURE [Part::FeaturePython] Slice003_child2001  label="Slice003.023"  # WARN: FeaturePython — macro-defined, semantics opaque (R4)
  Base = -> Slice003
  FilterType = 1
  Invert = false
  OverrideMaxVal = 0
  WindowFrom = 80
  WindowTo = 100
  items = 2
FEATURE [App::DocumentObjectGroup] GrExplode_Slice003  label="Exploded Slice003"
  Group = -> [Slice003_child0022,Slice003_child2001]
FEATURE [Part::Part2DObjectPython] Rectangle006  # Draft 2D object (typed FeaturePython)
  ChamferSize = 0
  Columns = 1
  FilletRadius = 0
  Height = 188
  Length = 140
  MakeFace = true
  Placement = pos=(64.6826,-163.503,-57.4031) rot=(-1,0,0;1.5708rad)
  Rows = 1
  Support = -> [Slice003_child0022]
FEATURE [Part::FeaturePython] Slice004  # WARN: FeaturePython — macro-defined, semantics opaque (R4)
  Base = -> Slice003_child0022
  Mode = 1
  Tolerance = 0
  Tools = -> [Rectangle006]
FEATURE [Part::FeaturePython] Slice004_child0006  label="Slice004.006"  # WARN: FeaturePython — macro-defined, semantics opaque (R4)
  Base = -> Slice004
  FilterType = 1
  Invert = false
  OverrideMaxVal = 0
  WindowFrom = 80
  WindowTo = 100
  items = 0
FEATURE [Part::FeaturePython] Slice004_child1001  label="Slice004.007"  # WARN: FeaturePython — macro-defined, semantics opaque (R4)
  Base = -> Slice004
  FilterType = 1
  Invert = false
  OverrideMaxVal = 0
  WindowFrom = 80
  WindowTo = 100
  items = 1
FEATURE [Part::FeaturePython] Slice004_child2001  label="Slice004.008"  # WARN: FeaturePython — macro-defined, semantics opaque (R4)
  Base = -> Slice004
  FilterType = 1
  Invert = false
  OverrideMaxVal = 0
  WindowFrom = 80
  WindowTo = 100
  items = 2
FEATURE [Part::FeaturePython] Slice004_child3  label="Slice004.3"  # WARN: FeaturePython — macro-defined, semantics opaque (R4)
  Base = -> Slice004
  FilterType = 1
  Invert = false
  OverrideMaxVal = 0
  WindowFrom = 80
  WindowTo = 100
  items = 3
FEATURE [Part::FeaturePython] Slice004_child4  label="Slice004.4"  # WARN: FeaturePython — macro-defined, semantics opaque (R4)
  Base = -> Slice004
  FilterType = 1
  Invert = false
  OverrideMaxVal = 0
  WindowFrom = 80
  WindowTo = 100
  items = 4
FEATURE [App::DocumentObjectGroup] GrExplode_Slice004  label="Exploded Slice004"
  Group = -> [Slice004_child0006,Slice004_child1001,Slice004_child2001,Slice004_child3,Slice004_child4]
FEATURE [Part::Extrusion] Extrusion004
  Base = -> Wire
  Dir = (4.17798e-10,11,-4.14596e-10)
  DirMode = 0
  FaceMakerClass = Part::FaceMakerBullseye
  LengthFwd = 0
  LengthRev = 0
  Solid = true
  Symmetric = false
